# Revit family: DBLTD_TheSenatorGroup_OffcTbls_Play_AVMedia
name_source: partatom
category: Furniture
revit_build: Autodesk Revit 2018 (Build: 20170223_1515(x64)
units: mm (PartAtom-declared; Revit-internal decimal feet)

## family parameters
Always vertical = Yes
Cut with Voids When Loaded = No
Room Calculation Point = No
Shared = Yes
Work Plane-Based = No

## types (2) — shared parameters
AssetType = Movable
BIMObjectName = TheSenatorGroup_OfficeTables_Play_AVMedia
Category = Pr_40_50_21_60:Office tables
DimensionsHeight = 730 -1220mm
DimensionsPlanSize = 1200 x 2260 mm
DurationUnit = Years
ExpectedLife = 15
ExposedEdges = Matching
Finish = HD Highland Oak, BH Beech, MP Maple, WH White, AT Autumn. WK Winter Oak, SO Strata Oak, MC Mocha, HW Hacienda White, DN Denim, LY Clay, LS Lemon Sorbet, LG Light Grey, CW Carini Walnut
FrameSupports = Adjustable
FramesColour = Black
IfcExportAs = IfcFurnitureType
IfcExportType = TABLE
Keynote = Pr_40_50_21_60
Manufacturer = The Senator Group
ManufacturerName = The Senator Group
ManufacturerURL = https://www.thesenatorgroup.com
Material = MFC
NBSDescription = Office tables
NBSReference = 45-35-20/340
Name = OfficeTables_Play_AVMedia_TheSenatorGroup
NominalDepth = 2260 mm  [stored 7.4147 ft]
NominalHeight = 1800 mm  [stored 5.90551 ft]
NominalLength = 1200 mm  [stored 3.93701 ft]
NominalWidth = 1200 mm  [stored 3.93701 ft]
NumberOfChairs = 5
OmniClassCode = 22-12 51 23
OmniClassTitle = Office Tables
OmniClassVersion = Table 22 2012-05-16
ProductInformation = https://www.thesenatorgroup.com
ReplacementCost = 0
Shape = Rectangular
Size = L 2260mm x  W 1200mm x  H 730-1220mm
SustainabilityPerformance = Table top produced using FSC® certified timber
TableTopThickness = 25 mm  [stored 0.082021 ft]
URL = https://www.thesenatorgroup.com
Uniclass2015Code = Pr_40_50_21_60
Uniclass2015Title = Office tables
Uniclass2015Version = Products v1.9
Version = 1
WarrantyDescription = Senator warrants that its manufactured products are free from manufacturing defects - in materials or workmanship - for a period of ten (10) years on Senator Seating ranges; and fifteen (15) years on Senator Desking ranges
WarrantyDurationLabor = 15
WarrantyDurationParts = 15
WarrantyDurationUnit = Years
WarrantyGuarantorLabor = 15
WarrantyGuarantorParts = 15
WorksurfaceArea = 2.71 m²
zero-valued in all types: Cost

## per-type parameters (varying)
| type | Description | Features | Model | ModelNumber | WithCutout |
| AV Media 1200mm(w) x 2260mm(d) x 730-1220mm(h) | 1200mm x 2260mm AV Media Table | Height Adjustable | PYPAE2012 | PYPAE2012 | No |
| AV Media with Cutout 1200mm(w) x 2260mm(d) x 730-1220mm(h) | 1200mm x 2260mm AV Media Table with Cutout | Height Adjustable, with cutout for IDP | PYPAE201250 + PYPIDP50AV or PYPIDP50AVS | PYPAE201250 + PYPIDP50AV or PYPIDP50AVS | Yes |

note: column(s) folded — value = type name in every type: ModelReference

note: [stored X ft] marks values corroborated as IEEE doubles in the binary element streams (Revit-internal decimal feet)

## geometry (parser evidence)
native form markers: Sweep x1
no freeform markers — native parametric forms only
